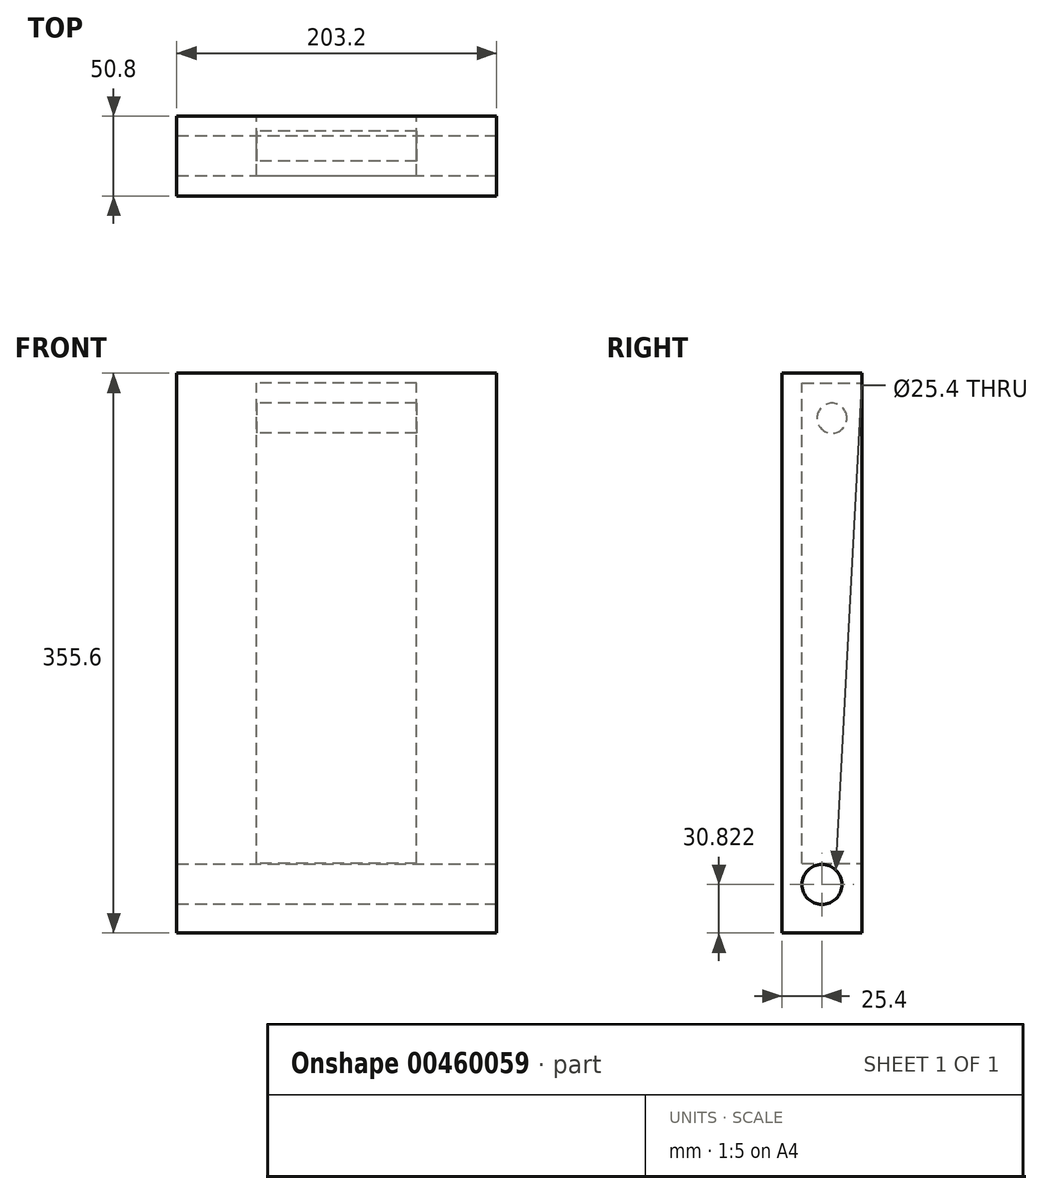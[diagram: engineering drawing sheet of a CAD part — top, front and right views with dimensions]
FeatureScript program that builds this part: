
annotation { "Feature Type Name" : "Feature", "Feature Type Description" : "" }
export const myFeature = defineFeature(function(context is Context, id is Id, definition is map)
    precondition{}
    {
        {
            var Q0;
            Q0=qCreatedBy(makeId("Right.planeOp"),FACE);
            var sketch = newSketch(context, id + "F0", { "sketchPlane" : qUnion([Q0])});
            skLineSegment(sketch, "E0.bottom", {"start": v(-25.4, -50.11) * mm, "end": v(25.4, -50.11) * mm});
            skLineSegment(sketch, "E0.top", {"start": v(-25.4, 305.49) * mm, "end": v(25.4, 305.49) * mm});
            skLineSegment(sketch, "E0.left", {"start": v(-25.4, -50.11) * mm, "end": v(-25.4, 305.49) * mm});
            skLineSegment(sketch, "E0.right", {"start": v(25.4, -50.11) * mm, "end": v(25.4, 305.49) * mm});
            skCircle(sketch, "E1", {"center": v(0, -19.29) * mm, "radius": 12.7 * mm});
            skSolve(sketch);
        }
        {
            var Q0;
            Q0 = qSketchRegion(id + "F0", true);
            extrude(context, id + "F1", {"entities" : qUnion([Q0]), "depth" : 101.6 * mm, "hasSecondDirection" : true, "secondDirectionOppositeDirection" : true, "secondDirectionDepth" : 101.6 * mm});
        }
        {
            var Q0;
            Q0=makeQuery(id+"F1.opExtrude","SWEPT_FACE",FACE,{"disambiguationData":[OSD([sQuery(id+"F0.wireOp",EDGE,"E0.right")])]});
            var sketch = newSketch(context, id + "F2", { "sketchPlane" : qUnion([Q0])});
            skLineSegment(sketch, "E2.bottom", {"start": v(-50.8, -5.91) * mm, "end": v(50.8, -5.91) * mm});
            skLineSegment(sketch, "E2.top", {"start": v(-50.8, 299.14) * mm, "end": v(50.8, 299.14) * mm});
            skLineSegment(sketch, "E2.left", {"start": v(-50.8, -5.91) * mm, "end": v(-50.8, 299.14) * mm});
            skLineSegment(sketch, "E2.right", {"start": v(50.8, -5.91) * mm, "end": v(50.8, 299.14) * mm});
            skSolve(sketch);
        }
        {
            var Q0;
            Q0 = qSketchRegion(id + "F2", true);
            extrude(context, id + "F3", {"entities" : qUnion([Q0]), "operationType" : NewBodyOperationType.REMOVE, "oppositeDirection" : true, "depth" : 38.1 * mm});
        }
        {
            var Q0;
            Q0=makeQuery(id+"F3.boolean.opBoolean","COPY",FACE,{"derivedFrom":makeQuery(id+"F3.opExtrude","SWEPT_FACE",FACE,{"disambiguationData":[OSD([sQuery(id+"F2.wireOp",EDGE,"E2.right")])]})});
            var sketch = newSketch(context, id + "F4", { "sketchPlane" : qUnion([Q0])});
            skCircle(sketch, "E3", {"center": v(6.35, 276.91) * mm, "radius": 9.53 * mm});
            skPoint(sketch, "E3.centerSnap0", {"position": v(6.35, 299.14) * mm});
            skSolve(sketch);
        }
        {
            var Q0;
            Q0 = qSketchRegion(id + "F4", true);
            var Q1;
            Q1=makeQuery(id+"F3.boolean.opBoolean","COPY",FACE,{"derivedFrom":makeQuery(id+"F3.opExtrude","SWEPT_FACE",FACE,{"disambiguationData":[OSD([sQuery(id+"F2.wireOp",EDGE,"E2.left")])]})});
            extrude(context, id + "F5", {"entities" : qUnion([Q0]), "operationType" : NewBodyOperationType.ADD, "endBound" : BoundingType.UP_TO_SURFACE, "endBoundEntityFace" : qUnion([Q1]), "depth" : 25.4 * mm});
        }
    });
